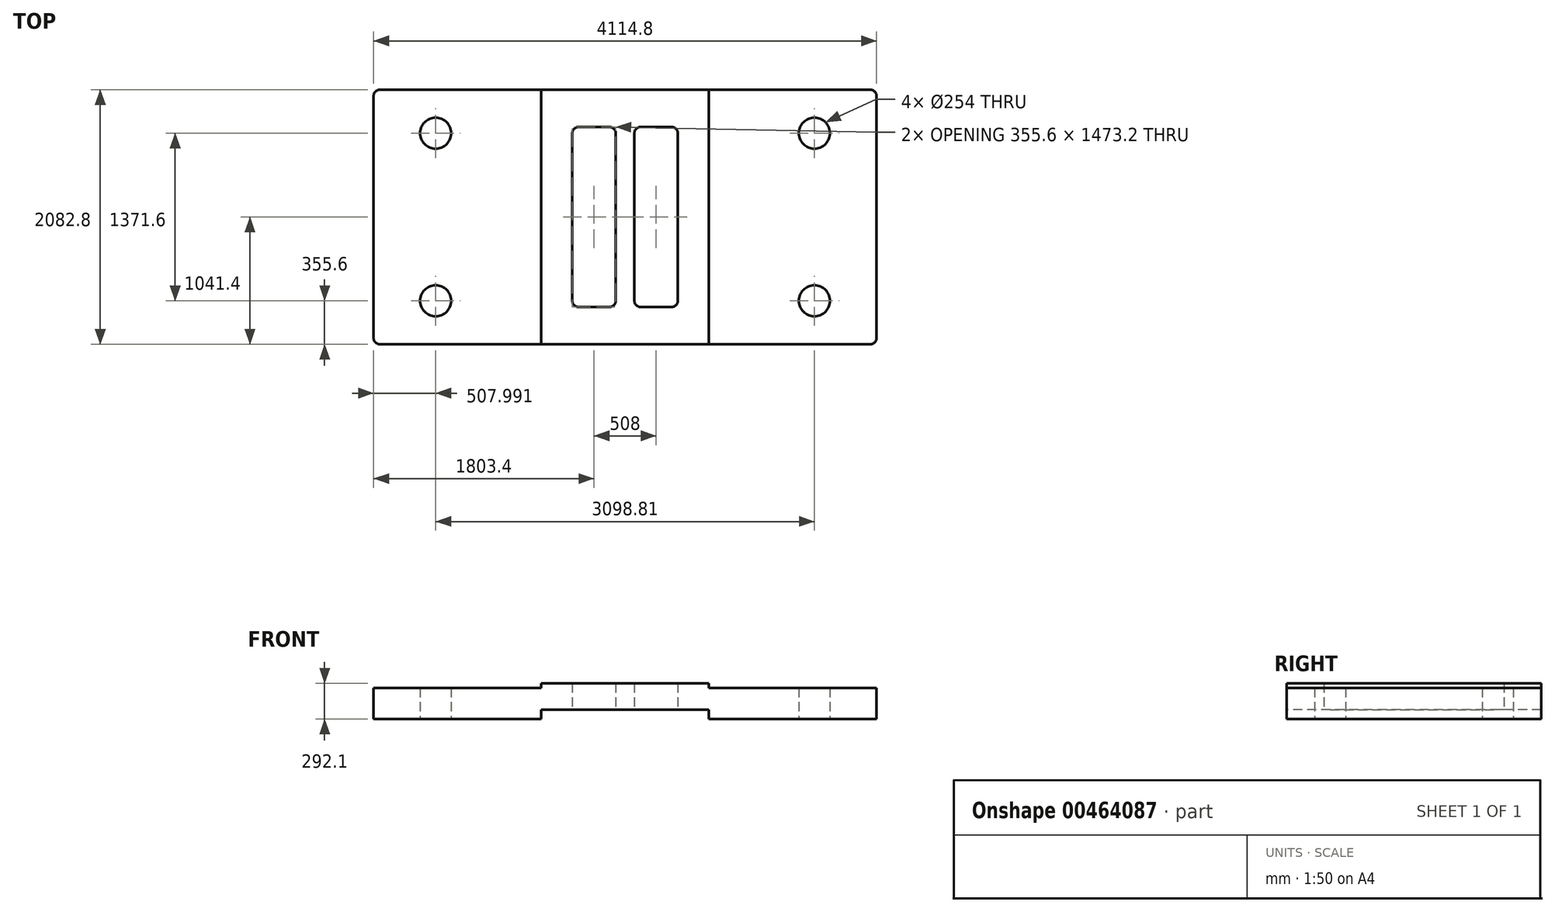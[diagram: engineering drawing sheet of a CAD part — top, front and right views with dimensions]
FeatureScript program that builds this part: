
annotation { "Feature Type Name" : "Feature", "Feature Type Description" : "" }
export const myFeature = defineFeature(function(context is Context, id is Id, definition is map)
    precondition{}
    {
        {
            var Q0;
            Q0=qCreatedBy(makeId("Top.planeOp"),FACE);
            var sketch = newSketch(context, id + "F0", { "sketchPlane" : qUnion([Q0])});
            skLineSegment(sketch, "E0.bottom", {"start": v(2006.6, 1041.4) * mm, "end": v(-2006.6, 1041.4) * mm});
            skLineSegment(sketch, "E0.top", {"start": v(2006.6, -1041.4) * mm, "end": v(-2006.6, -1041.4) * mm});
            skLineSegment(sketch, "E0.left", {"start": v(2057.4, 990.6) * mm, "end": v(2057.4, -990.6) * mm});
            skLineSegment(sketch, "E0.right", {"start": v(-2057.4, 990.6) * mm, "end": v(-2057.4, -990.6) * mm});
            skPoint(sketch, "E0.middle", {"position": v(0, 0) * mm});
            skPoint(sketch, "E1.visualSharp", {"position": v(-2057.4, 1041.4) * mm});
            skArc(sketch, "E1.filletArc", {"start": v(-2006.6, 1041.4) * mm, "mid": v(-2032.13, 1034.52) * mm, "end": v(-2050.74, 1015.75) * mm});
            skPoint(sketch, "E2.visualSharp", {"position": v(-2057.4, -1041.4) * mm});
            skArc(sketch, "E2.filletArc", {"start": v(-2057.4, -990.6) * mm, "mid": v(-2042.52, -1026.52) * mm, "end": v(-2006.6, -1041.4) * mm});
            skPoint(sketch, "E3.visualSharp", {"position": v(2057.4, 1041.4) * mm});
            skArc(sketch, "E3.filletArc", {"start": v(2057.4, 990.6) * mm, "mid": v(2042.52, 1026.52) * mm, "end": v(2006.6, 1041.4) * mm});
            skPoint(sketch, "E4.visualSharp", {"position": v(2057.4, -1041.4) * mm});
            skArc(sketch, "E4.filletArc", {"start": v(2006.6, -1041.4) * mm, "mid": v(2042.52, -1026.52) * mm, "end": v(2057.4, -990.6) * mm});
            skPoint(sketch, "E5.visualSharp", {"position": v(-2057.4, 990.6) * mm});
            skArc(sketch, "E5.filletArc", {"start": v(-2050.74, 1015.75) * mm, "mid": v(-2055.7, 1003.6) * mm, "end": v(-2057.4, 990.6) * mm});
            skLineSegment(sketch, "E6", {"start": v(-1676.4, -660.4) * mm, "end": v(-1676.4, -650.63) * mm});
            skCircle(sketch, "E7", {"center": v(1549.4, 685.8) * mm, "radius": 127 * mm});
            skPoint(sketch, "E8.orphan", {"position": v(-1676.4, -1041.4) * mm});
            skPoint(sketch, "E9.orphan", {"position": v(1701.8, 1041.4) * mm});
            skPoint(sketch, "E10.start.orphan", {"position": v(1701.8, 748.13) * mm});
            skPoint(sketch, "E11.end.orphan", {"position": v(1676.4, -748.49) * mm});
            skPoint(sketch, "E12.orphan", {"position": v(1676.4, -1041.4) * mm});
            skLineSegment(sketch, "E13", {"start": v(-685.8, 1041.4) * mm, "end": v(-685.8, -1041.4) * mm});
            skLineSegment(sketch, "E14", {"start": v(685.8, 1041.4) * mm, "end": v(685.8, -1041.4) * mm});
            skLineSegment(sketch, "E15", {"start": v(-685.8, 1041.4) * mm, "end": v(685.8, 1041.4) * mm});
            skLineSegment(sketch, "E16", {"start": v(-685.8, -1041.4) * mm, "end": v(685.8, -1041.4) * mm});
            skLineSegment(sketch, "E17.bottom", {"start": v(381, 736.6) * mm, "end": v(127, 736.6) * mm});
            skLineSegment(sketch, "E17.top", {"start": v(381, -736.6) * mm, "end": v(127, -736.6) * mm});
            skLineSegment(sketch, "E17.left", {"start": v(431.8, 685.8) * mm, "end": v(431.8, -685.8) * mm});
            skLineSegment(sketch, "E17.right", {"start": v(76.2, 685.8) * mm, "end": v(76.2, -685.8) * mm});
            skPoint(sketch, "E17.middle", {"position": v(254, 0) * mm});
            skLineSegment(sketch, "E18.bottom", {"start": v(-381, 736.6) * mm, "end": v(-127, 736.6) * mm});
            skLineSegment(sketch, "E18.top", {"start": v(-381, -736.6) * mm, "end": v(-127, -736.6) * mm});
            skLineSegment(sketch, "E18.left", {"start": v(-431.8, 685.8) * mm, "end": v(-431.8, -685.8) * mm});
            skLineSegment(sketch, "E18.right", {"start": v(-76.2, 685.8) * mm, "end": v(-76.2, -685.8) * mm});
            skPoint(sketch, "E18.middle", {"position": v(-254, 0) * mm});
            skPoint(sketch, "E19.visualSharp", {"position": v(-431.8, 736.6) * mm});
            skArc(sketch, "E19.filletArc", {"start": v(-381, 736.6) * mm, "mid": v(-416.92, 721.72) * mm, "end": v(-431.8, 685.8) * mm});
            skPoint(sketch, "E20.visualSharp", {"position": v(-76.2, 736.6) * mm});
            skArc(sketch, "E20.filletArc", {"start": v(-76.2, 685.8) * mm, "mid": v(-91.08, 721.72) * mm, "end": v(-127, 736.6) * mm});
            skPoint(sketch, "E21.visualSharp", {"position": v(-76.2, -736.6) * mm});
            skArc(sketch, "E21.filletArc", {"start": v(-127, -736.6) * mm, "mid": v(-91.08, -721.72) * mm, "end": v(-76.2, -685.8) * mm});
            skPoint(sketch, "E22.visualSharp", {"position": v(-431.8, -736.6) * mm});
            skArc(sketch, "E22.filletArc", {"start": v(-431.8, -685.8) * mm, "mid": v(-416.92, -721.72) * mm, "end": v(-381, -736.6) * mm});
            skPoint(sketch, "E23.visualSharp", {"position": v(76.2, 736.6) * mm});
            skArc(sketch, "E23.filletArc", {"start": v(127, 736.6) * mm, "mid": v(91.08, 721.72) * mm, "end": v(76.2, 685.8) * mm});
            skPoint(sketch, "E24.visualSharp", {"position": v(431.8, 736.6) * mm});
            skArc(sketch, "E24.filletArc", {"start": v(431.8, 685.8) * mm, "mid": v(416.92, 721.72) * mm, "end": v(381, 736.6) * mm});
            skPoint(sketch, "E25.visualSharp", {"position": v(431.8, -736.6) * mm});
            skArc(sketch, "E25.filletArc", {"start": v(381, -736.6) * mm, "mid": v(416.92, -721.72) * mm, "end": v(431.8, -685.8) * mm});
            skPoint(sketch, "E26.visualSharp", {"position": v(76.2, -736.6) * mm});
            skArc(sketch, "E26.filletArc", {"start": v(76.2, -685.8) * mm, "mid": v(91.08, -721.72) * mm, "end": v(127, -736.6) * mm});
            skLineSegment(sketch, "E27", {"start": v(-2057.4, 1041.4) * mm, "end": v(-1549.4, 1041.4) * mm});
            skCircle(sketch, "E28", {"center": v(-1549.4, 685.8) * mm, "radius": 127 * mm});
            skLineSegment(sketch, "E29", {"start": v(-2057.4, -1041.4) * mm, "end": v(-1549.4, -1041.4) * mm});
            skLineSegment(sketch, "E30", {"start": v(2057.4, -1041.4) * mm, "end": v(1549.4, -1041.4) * mm});
            skLineSegment(sketch, "E31", {"start": v(2057.4, 1041.4) * mm, "end": v(1549.4, 1041.4) * mm});
            skCircle(sketch, "E32", {"center": v(1549.4, -685.8) * mm, "radius": 127 * mm});
            skCircle(sketch, "E33", {"center": v(-1549.4, -685.8) * mm, "radius": 127 * mm});
            skSolve(sketch);
        }
        {
            var Q0;
            Q0=makeQuery(id+"F0.imprint","IMPRINT",FACE,{"disambiguationData":[TD([[makeQuery(id+"F0.imprint","IMPRINT",EDGE,{"derivedFrom":sQuery(id+"F0.wireOp",EDGE,"E13")}),1.0]])]});
            extrude(context, id + "F1", {"entities" : qUnion([Q0]), "endBound" : BoundingType.SYMMETRIC, "depth" : 330.2 * mm});
        }
        {
            var Q0;
            Q0 = qSketchRegion(id + "F0", true);
            extrude(context, id + "F2", {"entities" : qUnion([Q0]), "operationType" : NewBodyOperationType.ADD, "endBound" : BoundingType.SYMMETRIC, "depth" : 254 * mm});
        }
        {
            var Q0;
            {var subQ0=sQuery(id+"F0.wireOp",EDGE,"E16");Q0=makeQuery(id+"F2.boolean.opBoolean","MERGE",FACE,{"derivedFrom":[makeQuery(id+"F1.opExtrude","SWEPT_FACE",FACE,{"disambiguationData":[OSD([subQ0])]}),makeQuery(id+"F2.opExtrude","SWEPT_FACE",FACE,{"disambiguationData":[OSD([sQuery(id+"F0.wireOp",EDGE,"E0.top"),subQ0])]})]});}
            var sketch = newSketch(context, id + "F3", { "sketchPlane" : qUnion([Q0])});
            skLineSegment(sketch, "E34", {"start": v(-685.8, -165.1) * mm, "end": v(-685.8, -50.8) * mm});
            skLineSegment(sketch, "E35", {"start": v(685.8, -165.1) * mm, "end": v(685.8, -50.8) * mm});
            skLineSegment(sketch, "E36", {"start": v(-685.8, -50.8) * mm, "end": v(685.8, -50.8) * mm});
            skLineSegment(sketch, "E37", {"start": v(685.8, -165.1) * mm, "end": v(-685.8, -165.1) * mm});
            skSolve(sketch);
        }
        {
            var Q0;
            Q0 = qSketchRegion(id + "F3", true);
            extrude(context, id + "F4", {"entities" : qUnion([Q0]), "operationType" : NewBodyOperationType.REMOVE, "oppositeDirection" : true, "depth" : 2202.18 * mm});
        }
    });
